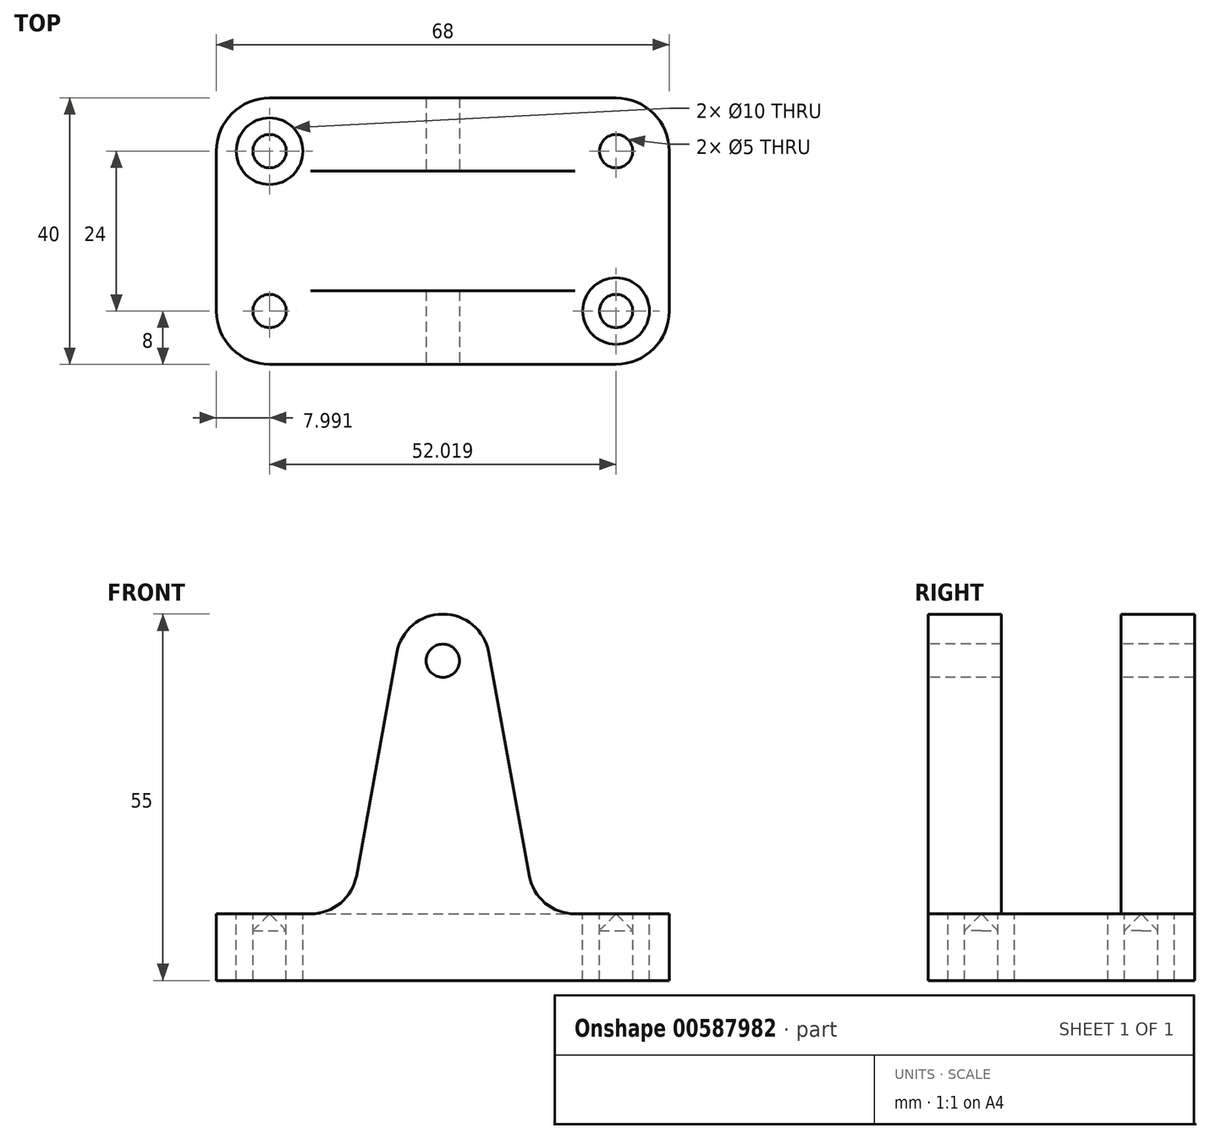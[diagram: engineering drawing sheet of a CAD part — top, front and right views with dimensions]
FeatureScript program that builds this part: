
annotation { "Feature Type Name" : "Feature", "Feature Type Description" : "" }
export const myFeature = defineFeature(function(context is Context, id is Id, definition is map)
    precondition{}
    {
        {
            var Q0;
            Q0=qCreatedBy(makeId("Front.planeOp"),FACE);
            var sketch = newSketch(context, id + "F0", { "sketchPlane" : qUnion([Q0])});
            skLineSegment(sketch, "E0", {"start": v(0, -39.8) * mm, "end": v(-34, -39.8) * mm});
            skLineSegment(sketch, "E1", {"start": v(0, -39.8) * mm, "end": v(34, -39.8) * mm});
            skLineSegment(sketch, "E2", {"start": v(34, -39.8) * mm, "end": v(34, -29.8) * mm});
            skLineSegment(sketch, "E3.MirrorCS", {"start": v(-34, -39.8) * mm, "end": v(-34, -29.8) * mm});
            skLineSegment(sketch, "E4", {"start": v(-34, -29.8) * mm, "end": v(34, -29.8) * mm});
            skLineSegment(sketch, "E5", {"start": v(0, -39.8) * mm, "end": v(0, 8.2) * mm, "construction": true});
            skCircle(sketch, "E6", {"center": v(0, 8.2) * mm, "radius": 2.5 * mm});
            skArc(sketch, "E7", {"start": v(6.89, 9.45) * mm, "mid": v(0, 15.2) * mm, "end": v(-6.89, 9.45) * mm});
            skLineSegment(sketch, "E8", {"start": v(14, -29.8) * mm, "end": v(6.89, 9.45) * mm});
            skLineSegment(sketch, "E9", {"start": v(-14, -29.8) * mm, "end": v(-6.89, 9.45) * mm});
            skSolve(sketch);
        }
        {
            var Q0;
            Q0=makeQuery(id+"F0.imprint","IMPRINT",FACE,{"disambiguationData":[TD([[makeQuery(id+"F0.imprint","IMPRINT",EDGE,{"derivedFrom":sQuery(id+"F0.wireOp",EDGE,"E6")}),-1.0]])]});
            var Q1;
            Q1=makeQuery(id+"F0.imprint","IMPRINT",FACE,{"disambiguationData":[TD([[makeQuery(id+"F0.imprint","IMPRINT",EDGE,{"derivedFrom":sQuery(id+"F0.wireOp",EDGE,"E0")}),-1.0]])]});
            extrude(context, id + "F1", {"entities" : qUnion([Q0, Q1]), "oppositeDirection" : true, "depth" : 40 * mm});
        }
        {
            var Q0;
            {var subQ0=sQuery(id+"F0.wireOp",EDGE,"E4");Q0=makeQuery(id+"F1.opExtrude","SWEPT_FACE",FACE,{"disambiguationData":[OSD([subQ0]),TDD([makeQuery(id+"F0.imprint","IMPRINT",EDGE,{"disambiguationData":[TD([[makeQuery(id+"F0.imprint","INTERSECT",VERTEX,{"derivedFrom":[sQuery(id+"F0.wireOp",EDGE,"E3.MirrorCS"),subQ0]}),-1.0]])],"derivedFrom":subQ0})])]});}
            var sketch = newSketch(context, id + "F2", { "sketchPlane" : qUnion([Q0])});
            skCircle(sketch, "E10.MirrorC", {"center": v(26, 32) * mm, "radius": 2.5 * mm});
            skCircle(sketch, "E11.MirrorC", {"center": v(26, 32) * mm, "radius": 5 * mm});
            skCircle(sketch, "E12.MirrorC", {"center": v(-26, 32) * mm, "radius": 2.5 * mm});
            skCircle(sketch, "E13.MirrorC", {"center": v(-26, 32) * mm, "radius": 5 * mm});
            skCircle(sketch, "E14.MirrorC", {"center": v(-26, 8) * mm, "radius": 2.5 * mm});
            skCircle(sketch, "E15.MirrorC", {"center": v(-26, 8) * mm, "radius": 5 * mm});
            skCircle(sketch, "E16.MirrorC", {"center": v(26, 8) * mm, "radius": 2.5 * mm});
            skCircle(sketch, "E17.MirrorC", {"center": v(26, 8) * mm, "radius": 5 * mm});
            skLineSegment(sketch, "E18", {"start": v(-26, 37) * mm, "end": v(-26, 27) * mm, "construction": true});
            skLineSegment(sketch, "E19", {"start": v(-26, 13) * mm, "end": v(-26, 3) * mm, "construction": true});
            skLineSegment(sketch, "E20", {"start": v(26, 37) * mm, "end": v(26, 27) * mm, "construction": true});
            skLineSegment(sketch, "E21", {"start": v(26, 13) * mm, "end": v(26, 3) * mm, "construction": true});
            skLineSegment(sketch, "E22", {"start": v(31, 8) * mm, "end": v(21, 8) * mm, "construction": true});
            skLineSegment(sketch, "E23", {"start": v(31, 32) * mm, "end": v(21, 32) * mm, "construction": true});
            skLineSegment(sketch, "E24", {"start": v(-31, 8) * mm, "end": v(-21, 8) * mm, "construction": true});
            skLineSegment(sketch, "E25", {"start": v(-31, 32) * mm, "end": v(-21, 32) * mm, "construction": true});
            skSolve(sketch);
        }
        {
            var Q0;
            Q0=qSketchRegion(id+"F2",true);
            extrude(context, id + "F3", {"entities" : qUnion([Q0]), "operationType" : NewBodyOperationType.REMOVE, "oppositeDirection" : true, "depth" : 3 * mm});
        }
        {
            var Q0;
            {var subQ1=sQuery(id+"F0.wireOp",EDGE,"E3.MirrorCS");var subQ5=sQuery(id+"F0.wireOp",EDGE,"E4");Q0=makeQuery(id+"F3.boolean.opBoolean","SPLIT",FACE,{"disambiguationData":[TD([makeQuery(id+"F1.opExtrude","SWEPT_FACE",FACE,{"disambiguationData":[OSD([subQ1])]})])],"derivedFrom":makeQuery(id+"F1.opExtrude","SWEPT_FACE",FACE,{"disambiguationData":[OSD([subQ5]),TDD([makeQuery(id+"F0.imprint","IMPRINT",EDGE,{"disambiguationData":[TD([[makeQuery(id+"F0.imprint","INTERSECT",VERTEX,{"derivedFrom":[subQ1,subQ5]}),-1.0]])],"derivedFrom":subQ5})])]})});}
            var sketch = newSketch(context, id + "F4", { "sketchPlane" : qUnion([Q0])});
            skLineSegment(sketch, "E26", {"start": v(-34, 0) * mm, "end": v(-34, 20) * mm, "construction": true});
            skLineSegment(sketch, "E27", {"start": v(-34, 20) * mm, "end": v(0, 20) * mm, "construction": true});
            skLineSegment(sketch, "E28", {"start": v(0, 20) * mm, "end": v(0, 32) * mm, "construction": true});
            skLineSegment(sketch, "E29", {"start": v(0, 20) * mm, "end": v(0, 8) * mm, "construction": true});
            skLineSegment(sketch, "E30", {"start": v(-18.64, 28.99) * mm, "end": v(18.64, 28.99) * mm});
            skLineSegment(sketch, "E31.MirrorCS", {"start": v(-18.64, 11.01) * mm, "end": v(18.64, 11.01) * mm});
            skLineSegment(sketch, "E32", {"start": v(18.64, 28.99) * mm, "end": v(18.64, 11.01) * mm});
            skLineSegment(sketch, "E33.MirrorCS", {"start": v(-18.64, 28.99) * mm, "end": v(-18.64, 11.01) * mm});
            skPoint(sketch, "E34.orphan", {"position": v(30, 28.99) * mm});
            skPoint(sketch, "E35.orphan", {"position": v(30, 11.01) * mm});
            skPoint(sketch, "E36.orphan", {"position": v(-30, 28.99) * mm});
            skPoint(sketch, "E37.orphan", {"position": v(-30, 11.01) * mm});
            skSolve(sketch);
        }
        {
            var Q0;
            {var subQ0=sQuery(id+"F4.wireOp",EDGE,"f66d0ab9-449e-4d87-a520-3055bb65471c0.MirrorCS");var subQ1=sQuery(id+"F4.wireOp",EDGE,"E30");var subQ2=makeQuery(id+"F4.imprint","INTERSECT",VERTEX,{"derivedFrom":[subQ1,subQ0]});Q0=makeQuery(id+"F4.imprint","IMPRINT",FACE,{"disambiguationData":[TD([[makeQuery(id+"F4.imprint","IMPRINT",EDGE,{"disambiguationData":[TD([[subQ2,1.0]])],"derivedFrom":subQ0}),1.0]])]});}
            var Q1;
            {var subQ0=sQuery(id+"F4.wireOp",EDGE,"E30");var subQ6=makeQuery(id+"F3.boolean.opBoolean","COPY",EDGE,{"derivedFrom":makeQuery(id+"F3.opExtrude","CAP_EDGE",EDGE,{"disambiguationData":[OSD([sQuery(id+"F2.wireOp",EDGE,"E13.MirrorC")])],"isStart":true})});var subQ11=makeQuery(id+"F4.imprint","INTERSECT",VERTEX,{"derivedFrom":[subQ6,subQ0]});Q1=makeQuery(id+"F4.imprint","IMPRINT",FACE,{"disambiguationData":[TD([[makeQuery(id+"F4.imprint","IMPRINT",EDGE,{"disambiguationData":[TD([[subQ11,-1.0]])],"derivedFrom":subQ0}),-1.0]])]});}
            extrude(context, id + "F5", {"entities" : qUnion([Q0, Q1]), "operationType" : NewBodyOperationType.REMOVE, "depth" : 50 * mm, "offsetDistance" : 25 * mm});
        }
        {
            var Q0;
            Q0=makeQuery(id+"F1.opExtrude","CAP_EDGE",EDGE,{"disambiguationData":[OSD([sQuery(id+"F0.wireOp",EDGE,"E3.MirrorCS")])],"isStart":true});
            var Q1;
            Q1=makeQuery(id+"F1.opExtrude","CAP_EDGE",EDGE,{"disambiguationData":[OSD([sQuery(id+"F0.wireOp",EDGE,"E2")])],"isStart":true});
            var Q2;
            Q2=makeQuery(id+"F1.opExtrude","CAP_EDGE",EDGE,{"disambiguationData":[OSD([sQuery(id+"F0.wireOp",EDGE,"E2")])],"isStart":false});
            var Q3;
            Q3=makeQuery(id+"F1.opExtrude","CAP_EDGE",EDGE,{"disambiguationData":[OSD([sQuery(id+"F0.wireOp",EDGE,"E3.MirrorCS")])],"isStart":false});
            fillet(context, id + "F6", {"entities" : qUnion([Q0, Q1, Q2, Q3]), "radius" : 8 * mm, "tangentPropagation" : true, "allowEdgeOverflow" : false});
        }
        {
            var Q0;
            Q0=makeQuery(id+"F3.boolean.opBoolean","COPY",FACE,{"derivedFrom":makeQuery(id+"F3.opExtrude","CAP_FACE",FACE,{"disambiguationData":[OSD([sQuery(id+"F2.wireOp",EDGE,"E12.MirrorC"),sQuery(id+"F2.wireOp",EDGE,"E13.MirrorC")])],"isStart":false})});
            var sketch = newSketch(context, id + "F7", { "sketchPlane" : qUnion([Q0])});
            skCircle(sketch, "E38", {"center": v(-26, 32) * mm, "radius": 2.5 * mm});
            skCircle(sketch, "E39", {"center": v(-26, 32) * mm, "radius": 5 * mm});
            skCircle(sketch, "E40.MirrorC", {"center": v(26, 32) * mm, "radius": 2.5 * mm});
            skCircle(sketch, "E41.MirrorC", {"center": v(26, 32) * mm, "radius": 5 * mm});
            skCircle(sketch, "E42.MirrorC", {"center": v(26, 8) * mm, "radius": 2.5 * mm});
            skCircle(sketch, "E43.MirrorC", {"center": v(26, 8) * mm, "radius": 5 * mm});
            skCircle(sketch, "E44.MirrorC", {"center": v(-26, 8) * mm, "radius": 2.5 * mm});
            skCircle(sketch, "E45.MirrorC", {"center": v(-26, 8) * mm, "radius": 5 * mm});
            skSolve(sketch);
        }
        {
            var Q0;
            Q0=makeQuery(id+"F0.imprint","IMPRINT",FACE,{"disambiguationData":[TD([[makeQuery(id+"F0.imprint","IMPRINT",EDGE,{"derivedFrom":sQuery(id+"F0.wireOp",EDGE,"E0")}),-1.0]])]});
            cPlane(context, id + "F8", {"entities" : qUnion([Q0]), "cplaneType" : CPlaneType.OFFSET, "offset" : 8 * mm, "oppositeDirection" : true, "width" : 150 * mm, "height" : 150 * mm});
        }
        {
            var Q0;
            {var subQ0=sQuery(id+"F0.wireOp",EDGE,"E9");var subQ1=sQuery(id+"F0.wireOp",EDGE,"E4");var subQ5=sQuery(id+"F4.wireOp",EDGE,"E31.MirrorCS");Q0=makeQuery(id+"F5.boolean.opBoolean","SPLIT",EDGE,{"disambiguationData":[TD([makeQuery(id+"F5.opExtrude","SWEPT_FACE",FACE,{"disambiguationData":[OSD([subQ5])]})])],"derivedFrom":makeQuery(id+"F1.opExtrude","SWEPT_EDGE",EDGE,{"disambiguationData":[OSD([subQ1,subQ0])]})});}
            var Q1;
            {var subQ0=sQuery(id+"F0.wireOp",EDGE,"E4");var subQ3=sQuery(id+"F0.wireOp",EDGE,"E9");var subQ5=sQuery(id+"F4.wireOp",EDGE,"E30");Q1=makeQuery(id+"F5.boolean.opBoolean","SPLIT",EDGE,{"disambiguationData":[TD([makeQuery(id+"F5.opExtrude","SWEPT_FACE",FACE,{"disambiguationData":[OSD([subQ5])]})])],"derivedFrom":makeQuery(id+"F1.opExtrude","SWEPT_EDGE",EDGE,{"disambiguationData":[OSD([subQ0,subQ3])]})});}
            var Q2;
            {var subQ0=sQuery(id+"F0.wireOp",EDGE,"E8");var subQ1=sQuery(id+"F0.wireOp",EDGE,"E4");var subQ5=sQuery(id+"F4.wireOp",EDGE,"E31.MirrorCS");Q2=makeQuery(id+"F5.boolean.opBoolean","SPLIT",EDGE,{"disambiguationData":[TD([makeQuery(id+"F5.opExtrude","SWEPT_FACE",FACE,{"disambiguationData":[OSD([subQ5])]})])],"derivedFrom":makeQuery(id+"F1.opExtrude","SWEPT_EDGE",EDGE,{"disambiguationData":[OSD([subQ1,subQ0])]})});}
            var Q3;
            {var subQ0=sQuery(id+"F0.wireOp",EDGE,"E8");var subQ1=sQuery(id+"F0.wireOp",EDGE,"E4");var subQ5=sQuery(id+"F4.wireOp",EDGE,"E30");Q3=makeQuery(id+"F5.boolean.opBoolean","SPLIT",EDGE,{"disambiguationData":[TD([makeQuery(id+"F5.opExtrude","SWEPT_FACE",FACE,{"disambiguationData":[OSD([subQ5])]})])],"derivedFrom":makeQuery(id+"F1.opExtrude","SWEPT_EDGE",EDGE,{"disambiguationData":[OSD([subQ1,subQ0])]})});}
            fillet(context, id + "F9", {"entities" : qUnion([Q0, Q1, Q2, Q3]), "radius" : 7 * mm, "tangentPropagation" : true, "allowEdgeOverflow" : false});
        }
        {
            var Q0;
            Q0=qSketchRegion(id+"F7",true);
            extrude(context, id + "F10", {"entities" : qUnion([Q0]), "operationType" : NewBodyOperationType.ADD, "depth" : 3 * mm, "offsetDistance" : 25 * mm});
        }
        {
            var Q0;
            Q0=makeQuery(id+"F2.imprint","IMPRINT",FACE,{"disambiguationData":[TD([[makeQuery(id+"F2.imprint","IMPRINT",EDGE,{"derivedFrom":sQuery(id+"F2.wireOp",EDGE,"E12.MirrorC")}),-1.0]])]});
            var Q1;
            Q1=makeQuery(id+"F2.imprint","IMPRINT",FACE,{"disambiguationData":[TD([[makeQuery(id+"F2.imprint","IMPRINT",EDGE,{"derivedFrom":sQuery(id+"F2.wireOp",EDGE,"E14.MirrorC")}),1.0]])]});
            var Q2;
            Q2=makeQuery(id+"F2.imprint","IMPRINT",FACE,{"disambiguationData":[TD([[makeQuery(id+"F2.imprint","IMPRINT",EDGE,{"derivedFrom":sQuery(id+"F2.wireOp",EDGE,"E16.MirrorC")}),-1.0]])]});
            var Q3;
            Q3=makeQuery(id+"F2.imprint","IMPRINT",FACE,{"disambiguationData":[TD([[makeQuery(id+"F2.imprint","IMPRINT",EDGE,{"derivedFrom":sQuery(id+"F2.wireOp",EDGE,"E10.MirrorC")}),1.0]])]});
            extrude(context, id + "F11", {"entities" : qUnion([Q0, Q1, Q2, Q3]), "operationType" : NewBodyOperationType.REMOVE, "oppositeDirection" : true, "depth" : 25 * mm, "offsetDistance" : 25 * mm});
        }
        {
            var Q0;
            Q0=makeQuery(id+"F11.boolean.opBoolean","COPY",EDGE,{"derivedFrom":makeQuery(id+"F11.opExtrude","CAP_EDGE",EDGE,{"disambiguationData":[OSD([sQuery(id+"F2.wireOp",EDGE,"E12.MirrorC")])],"isStart":true})});
            var Q1;
            Q1=makeQuery(id+"F11.boolean.opBoolean","COPY",EDGE,{"derivedFrom":makeQuery(id+"F11.opExtrude","CAP_EDGE",EDGE,{"disambiguationData":[OSD([sQuery(id+"F2.wireOp",EDGE,"E10.MirrorC")])],"isStart":true})});
            var Q2;
            Q2=makeQuery(id+"F11.boolean.opBoolean","COPY",EDGE,{"derivedFrom":makeQuery(id+"F11.opExtrude","CAP_EDGE",EDGE,{"disambiguationData":[OSD([sQuery(id+"F2.wireOp",EDGE,"E16.MirrorC")])],"isStart":true})});
            var Q3;
            Q3=makeQuery(id+"F11.boolean.opBoolean","COPY",EDGE,{"derivedFrom":makeQuery(id+"F11.opExtrude","CAP_EDGE",EDGE,{"disambiguationData":[OSD([sQuery(id+"F2.wireOp",EDGE,"E14.MirrorC")])],"isStart":true})});
            chamfer(context, id + "F12", {"entities" : qUnion([Q0, Q1, Q2, Q3]), "chamferType" : ChamferType.OFFSET_ANGLE, "width" : 2.5 * mm, "oppositeDirection" : false, "angle" : 45 * degree, "tangentPropagation" : true});
        }
    });
